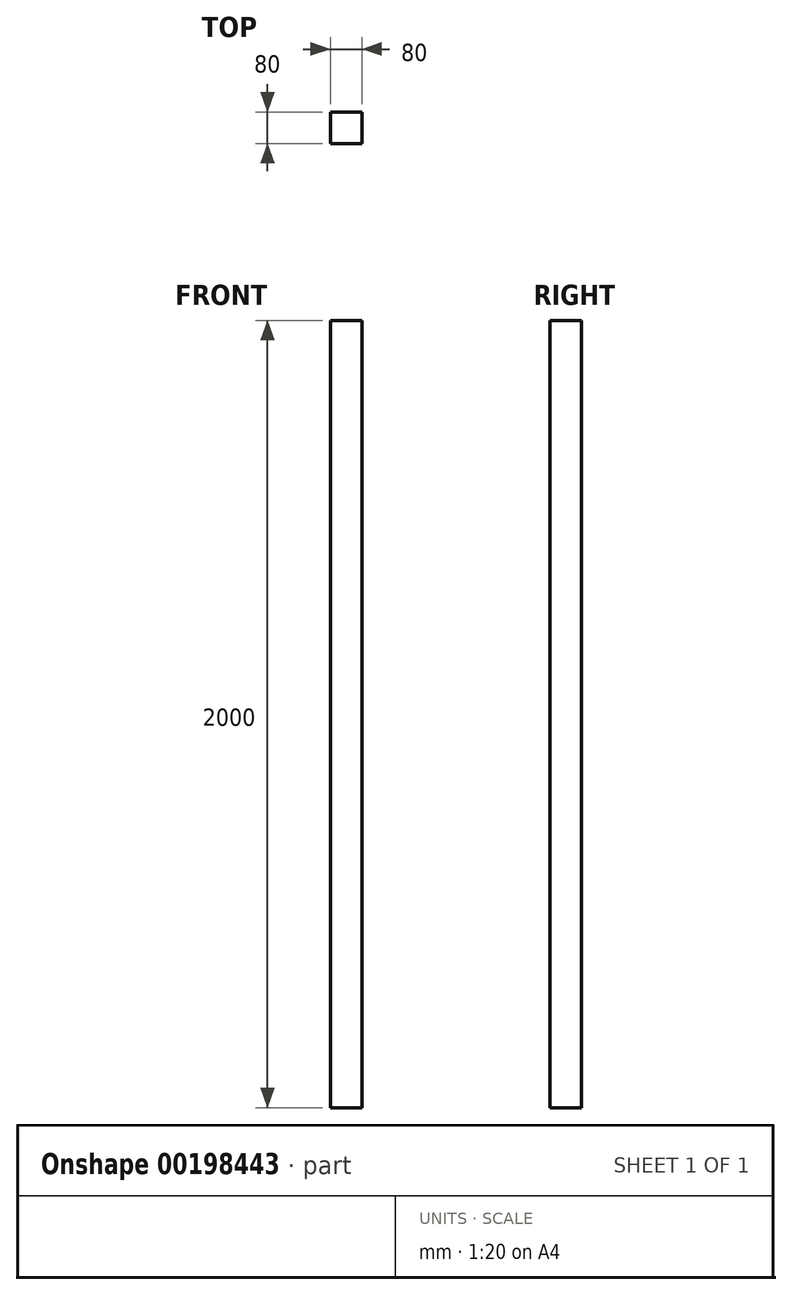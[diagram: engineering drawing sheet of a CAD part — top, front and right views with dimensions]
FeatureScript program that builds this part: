
annotation { "Feature Type Name" : "Feature", "Feature Type Description" : "" }
export const myFeature = defineFeature(function(context is Context, id is Id, definition is map)
    precondition{}
    {
        {
            var Q0;
            Q0=qCreatedBy(makeId("Top.planeOp"),FACE);
            var sketch = newSketch(context, id + "F0", { "sketchPlane" : qUnion([Q0])});
            skLineSegment(sketch, "E0.bottom", {"start": v(0, 0) * mm, "end": v(80, 0) * mm});
            skLineSegment(sketch, "E0.top", {"start": v(0, 80) * mm, "end": v(80, 80) * mm});
            skLineSegment(sketch, "E0.left", {"start": v(0, 0) * mm, "end": v(0, 80) * mm});
            skLineSegment(sketch, "E0.right", {"start": v(80, 0) * mm, "end": v(80, 80) * mm});
            skSolve(sketch);
        }
        {
            var Q0;
            Q0 = qSketchRegion(id + "F0", true);
            extrude(context, id + "F1", {"entities" : qUnion([Q0]), "depth" : 2000 * mm});
        }
    });
